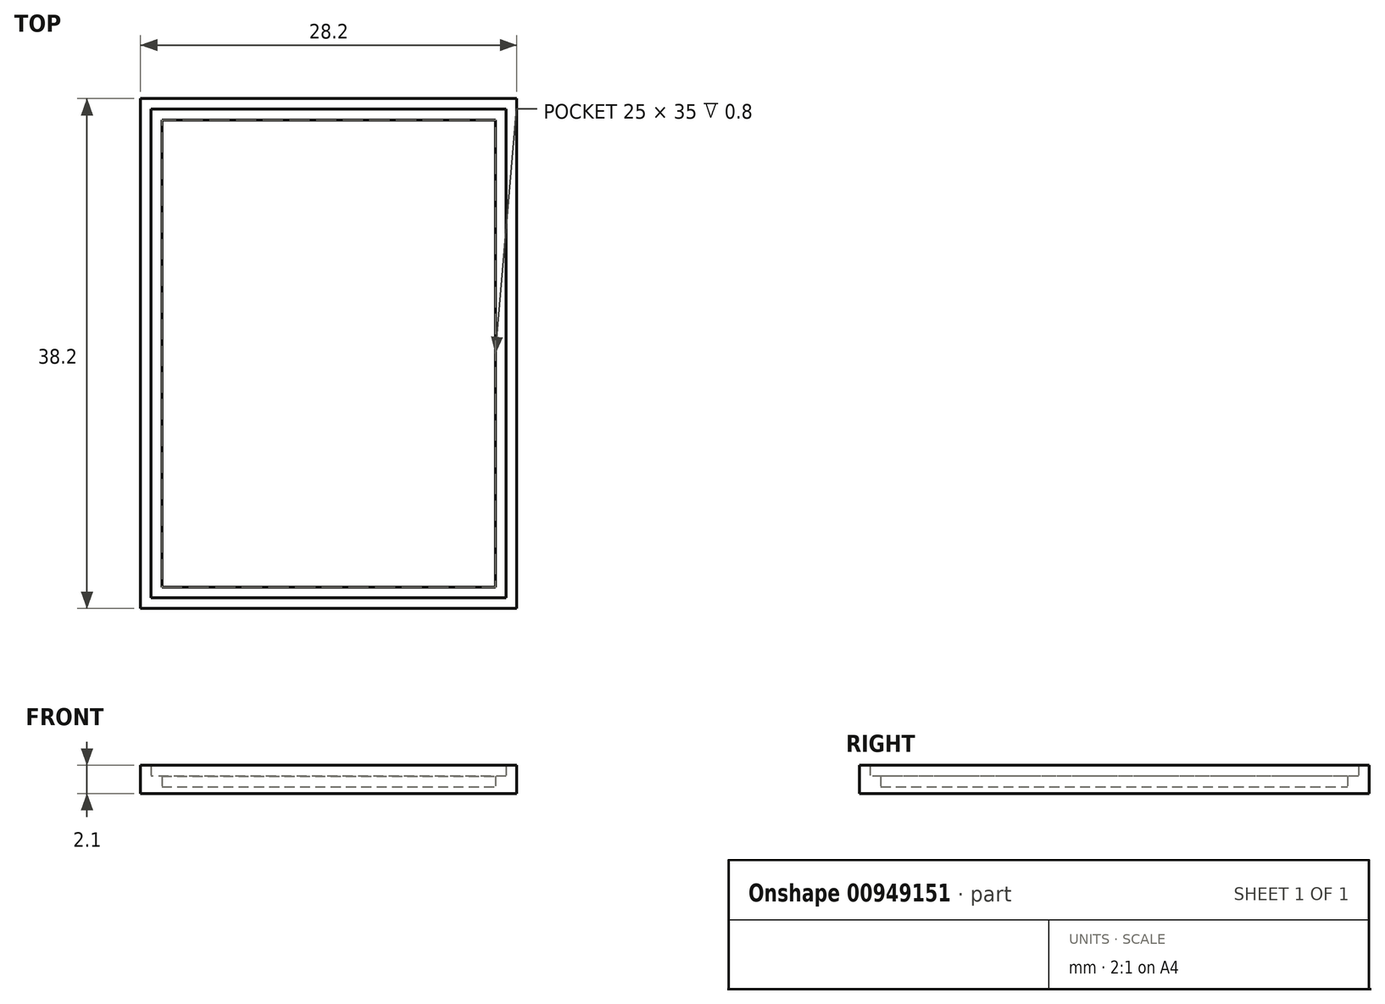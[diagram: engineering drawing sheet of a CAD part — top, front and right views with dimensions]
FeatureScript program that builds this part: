
annotation { "Feature Type Name" : "Feature", "Feature Type Description" : "" }
export const myFeature = defineFeature(function(context is Context, id is Id, definition is map)
    precondition{}
    {
        {
            var Q0;
            Q0=qCreatedBy(makeId("Top.planeOp"),FACE);
            var sketch = newSketch(context, id + "F0", { "sketchPlane" : qUnion([Q0])});
            skLineSegment(sketch, "E0.bottom", {"start": v(-12.5, 17.5) * mm, "end": v(12.5, 17.5) * mm});
            skLineSegment(sketch, "E0.top", {"start": v(-12.5, -17.5) * mm, "end": v(12.5, -17.5) * mm});
            skLineSegment(sketch, "E0.left", {"start": v(-12.5, 17.5) * mm, "end": v(-12.5, -17.5) * mm});
            skLineSegment(sketch, "E0.right", {"start": v(12.5, 17.5) * mm, "end": v(12.5, -17.5) * mm});
            skPoint(sketch, "E0.middle", {"position": v(0, 0) * mm});
            skSolve(sketch);
        }
        {
            var Q0;
            Q0=qCreatedBy(makeId("Front.planeOp"),FACE);
            var sketch = newSketch(context, id + "F1", { "sketchPlane" : qUnion([Q0])});
            skLineSegment(sketch, "E1", {"start": v(-12.5, 0) * mm, "end": v(-14.1, 0) * mm});
            skLineSegment(sketch, "E2", {"start": v(-14.1, 0) * mm, "end": v(-14.1, 1.6) * mm});
            skLineSegment(sketch, "E3", {"start": v(-14.1, 1.6) * mm, "end": v(-13.3, 1.6) * mm});
            skLineSegment(sketch, "E4", {"start": v(-13.3, 1.6) * mm, "end": v(-13.3, 0.8) * mm});
            skLineSegment(sketch, "E5", {"start": v(-13.3, 0.8) * mm, "end": v(-12.5, 0.8) * mm});
            skLineSegment(sketch, "E6", {"start": v(-12.5, 0.8) * mm, "end": v(-12.5, 0) * mm});
            skSolve(sketch);
        }
        {
            var Q0;
            Q0=makeQuery(id+"F1.imprint","IMPRINT",FACE,{"disambiguationData":[TD([[makeQuery(id+"F1.imprint","IMPRINT",EDGE,{"derivedFrom":sQuery(id+"F1.wireOp",EDGE,"E1")}),-1.0]])]});
            var Q1;
            Q1=sQuery(id+"F0.wireOp",EDGE,"E0.left");
            var Q2;
            Q2=sQuery(id+"F0.wireOp",EDGE,"E0.bottom");
            var Q3;
            Q3=sQuery(id+"F0.wireOp",EDGE,"E0.right");
            var Q4;
            Q4=sQuery(id+"F0.wireOp",EDGE,"E0.top");
            sweep(context, id + "F2", {"profiles" : qUnion([Q0]), "path" : qUnion([Q1, Q2, Q3, Q4])});
        }
        {
            var Q0;
            Q0=makeQuery(id+"F2.opSweep","SWEPT_FACE",FACE,{"disambiguationData":[OSD([sQuery(id+"F0.wireOp",EDGE,"E0.top"),sQuery(id+"F1.wireOp",EDGE,"E1")])]});
            var sketch = newSketch(context, id + "F3", { "sketchPlane" : qUnion([Q0])});
            skLineSegment(sketch, "E7.bottom", {"start": v(-14.1, 19.1) * mm, "end": v(14.1, 19.1) * mm});
            skLineSegment(sketch, "E7.top", {"start": v(-14.1, -19.1) * mm, "end": v(14.1, -19.1) * mm});
            skLineSegment(sketch, "E7.left", {"start": v(-14.1, 19.1) * mm, "end": v(-14.1, -19.1) * mm});
            skLineSegment(sketch, "E7.right", {"start": v(14.1, 19.1) * mm, "end": v(14.1, -19.1) * mm});
            skSolve(sketch);
        }
        {
            var Q0;
            Q0 = qSketchRegion(id + "F3", true);
            extrude(context, id + "F4", {"entities" : qUnion([Q0]), "operationType" : NewBodyOperationType.ADD, "depth" : 0.5 * mm, "offsetDistance" : 25 * mm});
        }
    });
